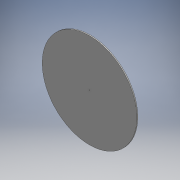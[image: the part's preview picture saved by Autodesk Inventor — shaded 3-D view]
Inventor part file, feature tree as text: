
AUTODESK INVENTOR PART (.ipt)
format: ipt  version: 2016 (Build 200138000, 138)  size: 96,768 bytes
history: native  units: mm
features: extrude x2, sketch x2
ambient origin geometry x8: Origin, YZ Plane, XZ Plane, XY Plane, X Axis, Y Axis, Z Axis, Center Point
bodies: Solid1 (feature_tree)
feature tree (4):
  extrude  "Extrusion1"  Depth=10.0mm TaperAngle=0.0deg
  extrude  "Extrusion2"  Depth=5.0mm TaperAngle=0.0deg
  sketch  "Sketch1"  dims[d0=1000.0mm d1=10.0mm d2=0.0mm]
  sketch  "Sketch2"  dims[d3=10.0mm d4=5.0mm d5=0.0mm]
